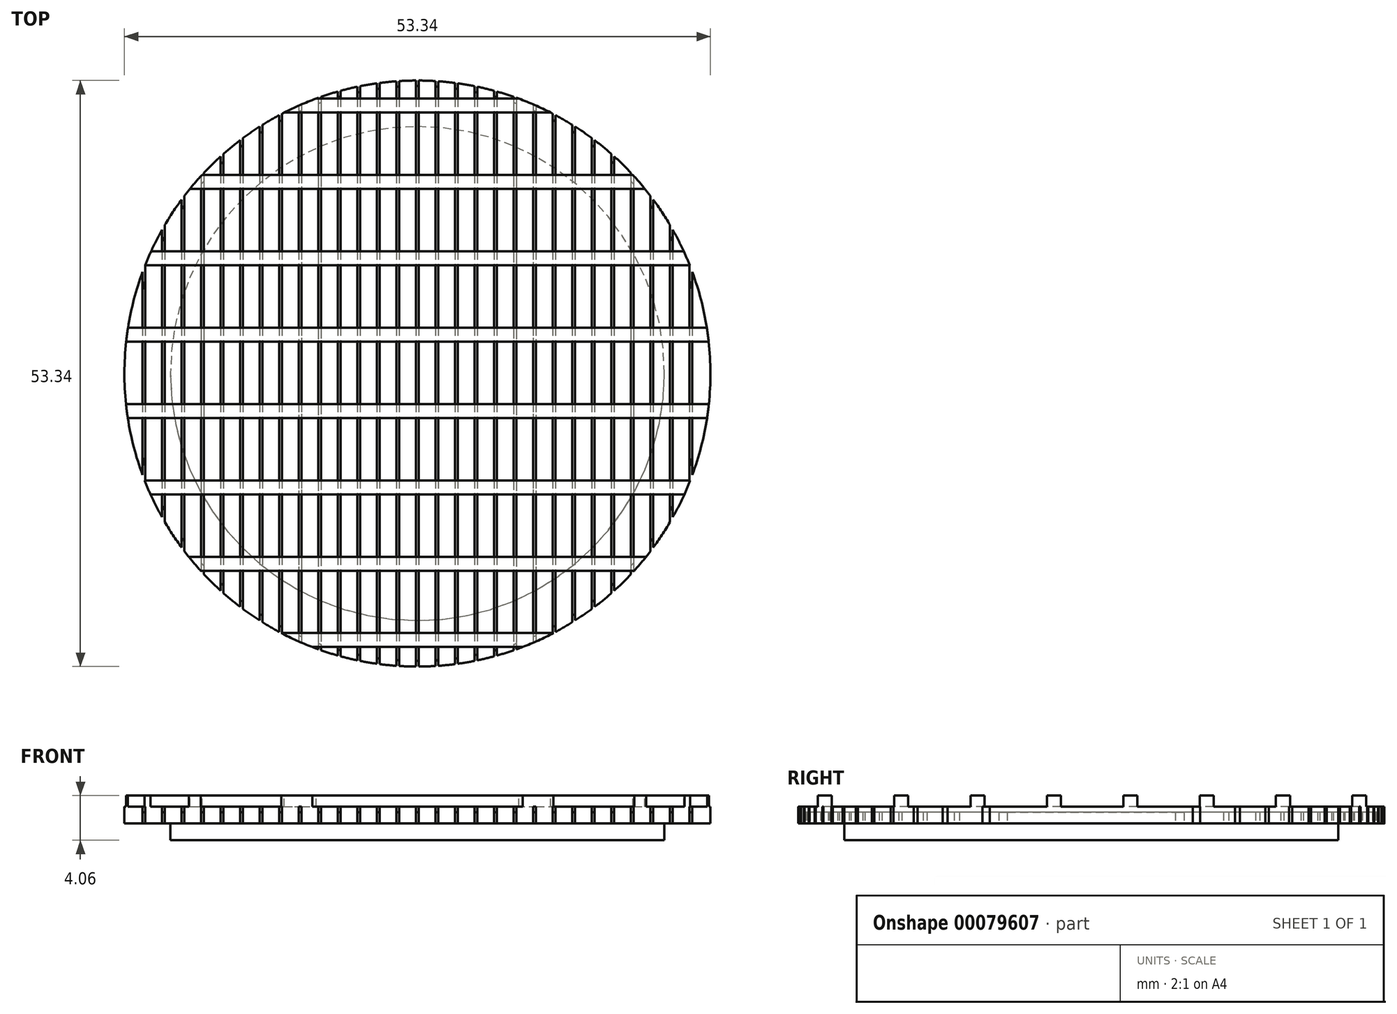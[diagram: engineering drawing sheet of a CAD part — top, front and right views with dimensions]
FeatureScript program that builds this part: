
annotation { "Feature Type Name" : "Feature", "Feature Type Description" : "" }
export const myFeature = defineFeature(function(context is Context, id is Id, definition is map)
    precondition{}
    {
        {
            var Q0;
            Q0=qCreatedBy(makeId("Top.planeOp"),FACE);
            var sketch = newSketch(context, id + "F0", { "sketchPlane" : qUnion([Q0])});
            skCircle(sketch, "E0", {"center": v(0, 0) * mm, "radius": 26.67 * mm});
            skSolve(sketch);
        }
        {
            var Q0;
            Q0 = qSketchRegion(id + "F0", true);
            extrude(context, id + "F1", {"entities" : qUnion([Q0]), "depth" : 1.52 * mm});
        }
        {
            var Q0;
            Q0=makeQuery(id+"F1.opExtrude","CAP_FACE",FACE,{"disambiguationData":[OSD([sQuery(id+"F0.wireOp",EDGE,"E0")])],"isStart":false});
            var sketch = newSketch(context, id + "F2", { "sketchPlane" : qUnion([Q0])});
            skLineSegment(sketch, "E1.bottom", {"start": v(-0.13, 27.42) * mm, "end": v(0.13, 27.42) * mm});
            skLineSegment(sketch, "E1.top", {"start": v(-0.13, -28.46) * mm, "end": v(0.13, -28.46) * mm});
            skLineSegment(sketch, "E1.left", {"start": v(-0.13, 27.42) * mm, "end": v(-0.13, -28.46) * mm});
            skLineSegment(sketch, "E1.right", {"start": v(0.13, 27.42) * mm, "end": v(0.13, -28.46) * mm});
            skLineSegment(sketch, "E2.1.0.0", {"start": v(1.65, 27.42) * mm, "end": v(1.9, 27.42) * mm});
            skLineSegment(sketch, "E2.1.0.1", {"start": v(1.9, 27.42) * mm, "end": v(1.9, -28.46) * mm});
            skLineSegment(sketch, "E2.1.0.2", {"start": v(1.65, 27.42) * mm, "end": v(1.65, -28.46) * mm});
            skLineSegment(sketch, "E2.1.0.3", {"start": v(1.65, -28.46) * mm, "end": v(1.9, -28.46) * mm});
            skLineSegment(sketch, "E2.2.0.0", {"start": v(3.43, 27.42) * mm, "end": v(3.68, 27.42) * mm});
            skLineSegment(sketch, "E2.2.0.1", {"start": v(3.68, 27.42) * mm, "end": v(3.68, -28.46) * mm});
            skLineSegment(sketch, "E2.2.0.2", {"start": v(3.43, 27.42) * mm, "end": v(3.43, -28.46) * mm});
            skLineSegment(sketch, "E2.2.0.3", {"start": v(3.43, -28.46) * mm, "end": v(3.68, -28.46) * mm});
            skLineSegment(sketch, "E2.3.0.0", {"start": v(5.2, 27.42) * mm, "end": v(5.46, 27.42) * mm});
            skLineSegment(sketch, "E2.3.0.1", {"start": v(5.46, 27.42) * mm, "end": v(5.46, -28.46) * mm});
            skLineSegment(sketch, "E2.3.0.2", {"start": v(5.2, 27.42) * mm, "end": v(5.2, -28.46) * mm});
            skLineSegment(sketch, "E2.3.0.3", {"start": v(5.2, -28.46) * mm, "end": v(5.46, -28.46) * mm});
            skLineSegment(sketch, "E2.4.0.0", {"start": v(6.98, 27.42) * mm, "end": v(7.24, 27.42) * mm});
            skLineSegment(sketch, "E2.4.0.1", {"start": v(7.24, 27.42) * mm, "end": v(7.24, -28.46) * mm});
            skLineSegment(sketch, "E2.4.0.2", {"start": v(6.98, 27.42) * mm, "end": v(6.99, -28.46) * mm});
            skLineSegment(sketch, "E2.4.0.3", {"start": v(6.99, -28.46) * mm, "end": v(7.24, -28.46) * mm});
            skLineSegment(sketch, "E2.5.0.0", {"start": v(8.76, 27.42) * mm, "end": v(9.02, 27.42) * mm});
            skLineSegment(sketch, "E2.5.0.1", {"start": v(9.02, 27.42) * mm, "end": v(9.02, -28.46) * mm});
            skLineSegment(sketch, "E2.5.0.2", {"start": v(8.76, 27.42) * mm, "end": v(8.76, -28.46) * mm});
            skLineSegment(sketch, "E2.5.0.3", {"start": v(8.76, -28.46) * mm, "end": v(9.02, -28.46) * mm});
            skLineSegment(sketch, "E2.6.0.0", {"start": v(10.54, 27.42) * mm, "end": v(10.8, 27.42) * mm});
            skLineSegment(sketch, "E2.6.0.1", {"start": v(10.8, 27.42) * mm, "end": v(10.8, -28.46) * mm});
            skLineSegment(sketch, "E2.6.0.2", {"start": v(10.54, 27.42) * mm, "end": v(10.54, -28.46) * mm});
            skLineSegment(sketch, "E2.6.0.3", {"start": v(10.54, -28.46) * mm, "end": v(10.8, -28.46) * mm});
            skLineSegment(sketch, "E2.7.0.0", {"start": v(12.32, 27.42) * mm, "end": v(12.57, 27.42) * mm});
            skLineSegment(sketch, "E2.7.0.1", {"start": v(12.57, 27.42) * mm, "end": v(12.57, -28.46) * mm});
            skLineSegment(sketch, "E2.7.0.2", {"start": v(12.32, 27.42) * mm, "end": v(12.32, -28.46) * mm});
            skLineSegment(sketch, "E2.7.0.3", {"start": v(12.32, -28.46) * mm, "end": v(12.57, -28.46) * mm});
            skLineSegment(sketch, "E2.8.0.0", {"start": v(14.1, 27.42) * mm, "end": v(14.35, 27.42) * mm});
            skLineSegment(sketch, "E2.8.0.1", {"start": v(14.35, 27.42) * mm, "end": v(14.35, -28.46) * mm});
            skLineSegment(sketch, "E2.8.0.2", {"start": v(14.1, 27.42) * mm, "end": v(14.1, -28.46) * mm});
            skLineSegment(sketch, "E2.8.0.3", {"start": v(14.1, -28.46) * mm, "end": v(14.35, -28.46) * mm});
            skLineSegment(sketch, "E2.9.0.0", {"start": v(15.88, 27.42) * mm, "end": v(16.13, 27.42) * mm});
            skLineSegment(sketch, "E2.9.0.1", {"start": v(16.13, 27.42) * mm, "end": v(16.13, -28.46) * mm});
            skLineSegment(sketch, "E2.9.0.2", {"start": v(15.88, 27.42) * mm, "end": v(15.88, -28.46) * mm});
            skLineSegment(sketch, "E2.9.0.3", {"start": v(15.88, -28.46) * mm, "end": v(16.13, -28.46) * mm});
            skLineSegment(sketch, "E2.10.0.0", {"start": v(17.65, 27.42) * mm, "end": v(17.9, 27.42) * mm});
            skLineSegment(sketch, "E2.10.0.1", {"start": v(17.9, 27.42) * mm, "end": v(17.9, -28.46) * mm});
            skLineSegment(sketch, "E2.10.0.2", {"start": v(17.65, 27.42) * mm, "end": v(17.65, -28.46) * mm});
            skLineSegment(sketch, "E2.10.0.3", {"start": v(17.65, -28.46) * mm, "end": v(17.9, -28.46) * mm});
            skLineSegment(sketch, "E2.11.0.0", {"start": v(19.43, 27.42) * mm, "end": v(19.69, 27.42) * mm});
            skLineSegment(sketch, "E2.11.0.1", {"start": v(19.69, 27.42) * mm, "end": v(19.69, -28.46) * mm});
            skLineSegment(sketch, "E2.11.0.2", {"start": v(19.43, 27.42) * mm, "end": v(19.43, -28.46) * mm});
            skLineSegment(sketch, "E2.11.0.3", {"start": v(19.43, -28.46) * mm, "end": v(19.69, -28.46) * mm});
            skLineSegment(sketch, "E2.12.0.0", {"start": v(21.2, 27.42) * mm, "end": v(21.46, 27.42) * mm});
            skLineSegment(sketch, "E2.12.0.1", {"start": v(21.46, 27.42) * mm, "end": v(21.46, -28.46) * mm});
            skLineSegment(sketch, "E2.12.0.2", {"start": v(21.2, 27.42) * mm, "end": v(21.2, -28.46) * mm});
            skLineSegment(sketch, "E2.12.0.3", {"start": v(21.2, -28.46) * mm, "end": v(21.46, -28.46) * mm});
            skLineSegment(sketch, "E2.13.0.0", {"start": v(22.99, 27.42) * mm, "end": v(23.24, 27.42) * mm});
            skLineSegment(sketch, "E2.13.0.1", {"start": v(23.24, 27.42) * mm, "end": v(23.24, -28.46) * mm});
            skLineSegment(sketch, "E2.13.0.2", {"start": v(22.99, 27.42) * mm, "end": v(22.99, -28.46) * mm});
            skLineSegment(sketch, "E2.13.0.3", {"start": v(22.99, -28.46) * mm, "end": v(23.24, -28.46) * mm});
            skLineSegment(sketch, "E2.14.0.0", {"start": v(24.77, 27.42) * mm, "end": v(25.02, 27.42) * mm});
            skLineSegment(sketch, "E2.14.0.1", {"start": v(25.02, 27.42) * mm, "end": v(25.02, -28.46) * mm});
            skLineSegment(sketch, "E2.14.0.2", {"start": v(24.77, 27.42) * mm, "end": v(24.77, -28.46) * mm});
            skLineSegment(sketch, "E2.14.0.3", {"start": v(24.77, -28.46) * mm, "end": v(25.02, -28.46) * mm});
            skLineSegment(sketch, "E2.direction1", {"start": v(-0.13, 27.42) * mm, "end": v(1.65, 27.42) * mm, "construction": true});
            skLineSegment(sketch, "E3.1.0.0", {"start": v(-1.9, 27.42) * mm, "end": v(-1.65, 27.42) * mm});
            skLineSegment(sketch, "E3.1.0.1", {"start": v(-1.9, 27.42) * mm, "end": v(-1.9, -28.46) * mm});
            skLineSegment(sketch, "E3.1.0.2", {"start": v(-1.65, 27.42) * mm, "end": v(-1.65, -28.46) * mm});
            skLineSegment(sketch, "E3.1.0.3", {"start": v(-1.9, -28.46) * mm, "end": v(-1.65, -28.46) * mm});
            skLineSegment(sketch, "E3.2.0.0", {"start": v(-3.68, 27.42) * mm, "end": v(-3.43, 27.42) * mm});
            skLineSegment(sketch, "E3.2.0.1", {"start": v(-3.68, 27.42) * mm, "end": v(-3.68, -28.46) * mm});
            skLineSegment(sketch, "E3.2.0.2", {"start": v(-3.43, 27.42) * mm, "end": v(-3.43, -28.46) * mm});
            skLineSegment(sketch, "E3.2.0.3", {"start": v(-3.68, -28.46) * mm, "end": v(-3.43, -28.46) * mm});
            skLineSegment(sketch, "E3.3.0.0", {"start": v(-5.46, 27.42) * mm, "end": v(-5.2, 27.42) * mm});
            skLineSegment(sketch, "E3.3.0.1", {"start": v(-5.46, 27.42) * mm, "end": v(-5.46, -28.46) * mm});
            skLineSegment(sketch, "E3.3.0.2", {"start": v(-5.2, 27.42) * mm, "end": v(-5.2, -28.46) * mm});
            skLineSegment(sketch, "E3.3.0.3", {"start": v(-5.46, -28.46) * mm, "end": v(-5.2, -28.46) * mm});
            skLineSegment(sketch, "E3.4.0.0", {"start": v(-7.24, 27.42) * mm, "end": v(-6.98, 27.42) * mm});
            skLineSegment(sketch, "E3.4.0.1", {"start": v(-7.24, 27.42) * mm, "end": v(-7.24, -28.46) * mm});
            skLineSegment(sketch, "E3.4.0.2", {"start": v(-6.98, 27.42) * mm, "end": v(-6.98, -28.46) * mm});
            skLineSegment(sketch, "E3.4.0.3", {"start": v(-7.24, -28.46) * mm, "end": v(-6.98, -28.46) * mm});
            skLineSegment(sketch, "E3.5.0.0", {"start": v(-9.02, 27.42) * mm, "end": v(-8.76, 27.42) * mm});
            skLineSegment(sketch, "E3.5.0.1", {"start": v(-9.02, 27.42) * mm, "end": v(-9.02, -28.46) * mm});
            skLineSegment(sketch, "E3.5.0.2", {"start": v(-8.76, 27.42) * mm, "end": v(-8.76, -28.46) * mm});
            skLineSegment(sketch, "E3.5.0.3", {"start": v(-9.02, -28.46) * mm, "end": v(-8.76, -28.46) * mm});
            skLineSegment(sketch, "E3.6.0.0", {"start": v(-10.8, 27.42) * mm, "end": v(-10.54, 27.42) * mm});
            skLineSegment(sketch, "E3.6.0.1", {"start": v(-10.8, 27.42) * mm, "end": v(-10.8, -28.46) * mm});
            skLineSegment(sketch, "E3.6.0.2", {"start": v(-10.54, 27.42) * mm, "end": v(-10.54, -28.46) * mm});
            skLineSegment(sketch, "E3.6.0.3", {"start": v(-10.8, -28.46) * mm, "end": v(-10.54, -28.46) * mm});
            skLineSegment(sketch, "E3.7.0.0", {"start": v(-12.57, 27.42) * mm, "end": v(-12.32, 27.42) * mm});
            skLineSegment(sketch, "E3.7.0.1", {"start": v(-12.57, 27.42) * mm, "end": v(-12.57, -28.46) * mm});
            skLineSegment(sketch, "E3.7.0.2", {"start": v(-12.32, 27.42) * mm, "end": v(-12.32, -28.46) * mm});
            skLineSegment(sketch, "E3.7.0.3", {"start": v(-12.57, -28.46) * mm, "end": v(-12.32, -28.46) * mm});
            skLineSegment(sketch, "E3.8.0.0", {"start": v(-14.35, 27.42) * mm, "end": v(-14.1, 27.42) * mm});
            skLineSegment(sketch, "E3.8.0.1", {"start": v(-14.35, 27.42) * mm, "end": v(-14.35, -28.46) * mm});
            skLineSegment(sketch, "E3.8.0.2", {"start": v(-14.1, 27.42) * mm, "end": v(-14.1, -28.46) * mm});
            skLineSegment(sketch, "E3.8.0.3", {"start": v(-14.35, -28.46) * mm, "end": v(-14.1, -28.46) * mm});
            skLineSegment(sketch, "E3.9.0.0", {"start": v(-16.13, 27.42) * mm, "end": v(-15.87, 27.42) * mm});
            skLineSegment(sketch, "E3.9.0.1", {"start": v(-16.13, 27.42) * mm, "end": v(-16.13, -28.46) * mm});
            skLineSegment(sketch, "E3.9.0.2", {"start": v(-15.87, 27.42) * mm, "end": v(-15.87, -28.46) * mm});
            skLineSegment(sketch, "E3.9.0.3", {"start": v(-16.13, -28.46) * mm, "end": v(-15.87, -28.46) * mm});
            skLineSegment(sketch, "E3.10.0.0", {"start": v(-17.9, 27.42) * mm, "end": v(-17.65, 27.42) * mm});
            skLineSegment(sketch, "E3.10.0.1", {"start": v(-17.9, 27.42) * mm, "end": v(-17.9, -28.46) * mm});
            skLineSegment(sketch, "E3.10.0.2", {"start": v(-17.65, 27.42) * mm, "end": v(-17.65, -28.46) * mm});
            skLineSegment(sketch, "E3.10.0.3", {"start": v(-17.9, -28.46) * mm, "end": v(-17.65, -28.46) * mm});
            skLineSegment(sketch, "E3.11.0.0", {"start": v(-19.68, 27.42) * mm, "end": v(-19.43, 27.42) * mm});
            skLineSegment(sketch, "E3.11.0.1", {"start": v(-19.68, 27.42) * mm, "end": v(-19.68, -28.46) * mm});
            skLineSegment(sketch, "E3.11.0.2", {"start": v(-19.43, 27.42) * mm, "end": v(-19.43, -28.46) * mm});
            skLineSegment(sketch, "E3.11.0.3", {"start": v(-19.68, -28.46) * mm, "end": v(-19.43, -28.46) * mm});
            skLineSegment(sketch, "E3.12.0.0", {"start": v(-21.46, 27.42) * mm, "end": v(-21.2, 27.42) * mm});
            skLineSegment(sketch, "E3.12.0.1", {"start": v(-21.46, 27.42) * mm, "end": v(-21.46, -28.46) * mm});
            skLineSegment(sketch, "E3.12.0.2", {"start": v(-21.2, 27.42) * mm, "end": v(-21.2, -28.46) * mm});
            skLineSegment(sketch, "E3.12.0.3", {"start": v(-21.46, -28.46) * mm, "end": v(-21.2, -28.46) * mm});
            skLineSegment(sketch, "E3.13.0.0", {"start": v(-23.24, 27.42) * mm, "end": v(-22.99, 27.42) * mm});
            skLineSegment(sketch, "E3.13.0.1", {"start": v(-23.24, 27.42) * mm, "end": v(-23.24, -28.46) * mm});
            skLineSegment(sketch, "E3.13.0.2", {"start": v(-22.99, 27.42) * mm, "end": v(-22.99, -28.46) * mm});
            skLineSegment(sketch, "E3.13.0.3", {"start": v(-23.24, -28.46) * mm, "end": v(-22.99, -28.46) * mm});
            skLineSegment(sketch, "E3.14.0.0", {"start": v(-25.02, 27.42) * mm, "end": v(-24.76, 27.42) * mm});
            skLineSegment(sketch, "E3.14.0.1", {"start": v(-25.02, 27.42) * mm, "end": v(-25.02, -28.46) * mm});
            skLineSegment(sketch, "E3.14.0.2", {"start": v(-24.76, 27.42) * mm, "end": v(-24.76, -28.46) * mm});
            skLineSegment(sketch, "E3.14.0.3", {"start": v(-25.02, -28.46) * mm, "end": v(-24.76, -28.46) * mm});
            skLineSegment(sketch, "E3.direction1", {"start": v(-0.13, 27.42) * mm, "end": v(-1.9, 27.42) * mm, "construction": true});
            skSolve(sketch);
        }
        {
            var Q0;
            Q0 = qSketchRegion(id + "F2", true);
            extrude(context, id + "F3", {"entities" : qUnion([Q0]), "operationType" : NewBodyOperationType.REMOVE, "endBound" : BoundingType.THROUGH_ALL, "oppositeDirection" : true, "depth" : 0.5 * mm});
        }
        {
            var Q0;
            Q0=qCreatedBy(makeId("Top.planeOp"),FACE);
            var sketch = newSketch(context, id + "F4", { "sketchPlane" : qUnion([Q0])});
            skCircle(sketch, "E4", {"center": v(0, 0) * mm, "radius": 26.16 * mm});
            skSolve(sketch);
        }
        {
            var Q0;
            Q0 = qSketchRegion(id + "F4", true);
            extrude(context, id + "F5", {"entities" : qUnion([Q0]), "operationType" : NewBodyOperationType.ADD, "depth" : 1.02 * mm});
        }
        {
            var Q0;
            {var subQ0=sQuery(id+"F0.wireOp",EDGE,"E0");var subQ2=makeQuery(id+"F1.opExtrude","CAP_FACE",FACE,{"disambiguationData":[OSD([subQ0])],"isStart":true});Q0=makeQuery(id+"F5.boolean.opBoolean","MERGE",FACE,{"derivedFrom":[makeQuery(id+"F3.boolean.opBoolean","SPLIT",FACE,{"disambiguationData":[TD([makeQuery(id+"F3.opExtrude","SWEPT_FACE",FACE,{"disambiguationData":[OSD([sQuery(id+"F2.wireOp",EDGE,"E2.14.0.1")])]})])],"derivedFrom":subQ2}),makeQuery(id+"F3.boolean.opBoolean","SPLIT",FACE,{"disambiguationData":[TD([makeQuery(id+"F3.opExtrude","SWEPT_FACE",FACE,{"disambiguationData":[OSD([sQuery(id+"F2.wireOp",EDGE,"E3.14.0.1")])]})])],"derivedFrom":subQ2}),makeQuery(id+"F3.boolean.opBoolean","SPLIT",FACE,{"disambiguationData":[TD([makeQuery(id+"F3.opExtrude","SWEPT_FACE",FACE,{"disambiguationData":[OSD([sQuery(id+"F2.wireOp",EDGE,"E1.left")])]})])],"derivedFrom":subQ2}),makeQuery(id+"F3.boolean.opBoolean","SPLIT",FACE,{"disambiguationData":[TD([makeQuery(id+"F3.opExtrude","SWEPT_FACE",FACE,{"disambiguationData":[OSD([sQuery(id+"F2.wireOp",EDGE,"E1.right")])]})])],"derivedFrom":subQ2}),makeQuery(id+"F3.boolean.opBoolean","SPLIT",FACE,{"disambiguationData":[TD([makeQuery(id+"F3.opExtrude","SWEPT_FACE",FACE,{"disambiguationData":[OSD([sQuery(id+"F2.wireOp",EDGE,"E2.1.0.1")])]})])],"derivedFrom":subQ2}),makeQuery(id+"F3.boolean.opBoolean","SPLIT",FACE,{"disambiguationData":[TD([makeQuery(id+"F3.opExtrude","SWEPT_FACE",FACE,{"disambiguationData":[OSD([sQuery(id+"F2.wireOp",EDGE,"E2.2.0.1")])]})])],"derivedFrom":subQ2}),makeQuery(id+"F3.boolean.opBoolean","SPLIT",FACE,{"disambiguationData":[TD([makeQuery(id+"F3.opExtrude","SWEPT_FACE",FACE,{"disambiguationData":[OSD([sQuery(id+"F2.wireOp",EDGE,"E2.3.0.1")])]})])],"derivedFrom":subQ2}),makeQuery(id+"F3.boolean.opBoolean","SPLIT",FACE,{"disambiguationData":[TD([makeQuery(id+"F3.opExtrude","SWEPT_FACE",FACE,{"disambiguationData":[OSD([sQuery(id+"F2.wireOp",EDGE,"E2.4.0.1")])]})])],"derivedFrom":subQ2}),makeQuery(id+"F3.boolean.opBoolean","SPLIT",FACE,{"disambiguationData":[TD([makeQuery(id+"F3.opExtrude","SWEPT_FACE",FACE,{"disambiguationData":[OSD([sQuery(id+"F2.wireOp",EDGE,"E2.5.0.1")])]})])],"derivedFrom":subQ2}),makeQuery(id+"F3.boolean.opBoolean","SPLIT",FACE,{"disambiguationData":[TD([makeQuery(id+"F3.opExtrude","SWEPT_FACE",FACE,{"disambiguationData":[OSD([sQuery(id+"F2.wireOp",EDGE,"E2.6.0.1")])]})])],"derivedFrom":subQ2}),makeQuery(id+"F3.boolean.opBoolean","SPLIT",FACE,{"disambiguationData":[TD([makeQuery(id+"F3.opExtrude","SWEPT_FACE",FACE,{"disambiguationData":[OSD([sQuery(id+"F2.wireOp",EDGE,"E2.7.0.1")])]})])],"derivedFrom":subQ2}),makeQuery(id+"F3.boolean.opBoolean","SPLIT",FACE,{"disambiguationData":[TD([makeQuery(id+"F3.opExtrude","SWEPT_FACE",FACE,{"disambiguationData":[OSD([sQuery(id+"F2.wireOp",EDGE,"E2.8.0.1")])]})])],"derivedFrom":subQ2}),makeQuery(id+"F3.boolean.opBoolean","SPLIT",FACE,{"disambiguationData":[TD([makeQuery(id+"F3.opExtrude","SWEPT_FACE",FACE,{"disambiguationData":[OSD([sQuery(id+"F2.wireOp",EDGE,"E2.9.0.1")])]})])],"derivedFrom":subQ2}),makeQuery(id+"F3.boolean.opBoolean","SPLIT",FACE,{"disambiguationData":[TD([makeQuery(id+"F3.opExtrude","SWEPT_FACE",FACE,{"disambiguationData":[OSD([sQuery(id+"F2.wireOp",EDGE,"E2.10.0.1")])]})])],"derivedFrom":subQ2}),makeQuery(id+"F3.boolean.opBoolean","SPLIT",FACE,{"disambiguationData":[TD([makeQuery(id+"F3.opExtrude","SWEPT_FACE",FACE,{"disambiguationData":[OSD([sQuery(id+"F2.wireOp",EDGE,"E2.11.0.1")])]})])],"derivedFrom":subQ2}),makeQuery(id+"F3.boolean.opBoolean","SPLIT",FACE,{"disambiguationData":[TD([makeQuery(id+"F3.opExtrude","SWEPT_FACE",FACE,{"disambiguationData":[OSD([sQuery(id+"F2.wireOp",EDGE,"E2.12.0.1")])]})])],"derivedFrom":subQ2}),makeQuery(id+"F3.boolean.opBoolean","SPLIT",FACE,{"disambiguationData":[TD([makeQuery(id+"F3.opExtrude","SWEPT_FACE",FACE,{"disambiguationData":[OSD([sQuery(id+"F2.wireOp",EDGE,"E2.13.0.1")])]})])],"derivedFrom":subQ2}),makeQuery(id+"F3.boolean.opBoolean","SPLIT",FACE,{"disambiguationData":[TD([makeQuery(id+"F3.opExtrude","SWEPT_FACE",FACE,{"disambiguationData":[OSD([sQuery(id+"F2.wireOp",EDGE,"E3.1.0.1")])]})])],"derivedFrom":subQ2}),makeQuery(id+"F3.boolean.opBoolean","SPLIT",FACE,{"disambiguationData":[TD([makeQuery(id+"F3.opExtrude","SWEPT_FACE",FACE,{"disambiguationData":[OSD([sQuery(id+"F2.wireOp",EDGE,"E3.2.0.1")])]})])],"derivedFrom":subQ2}),makeQuery(id+"F3.boolean.opBoolean","SPLIT",FACE,{"disambiguationData":[TD([makeQuery(id+"F3.opExtrude","SWEPT_FACE",FACE,{"disambiguationData":[OSD([sQuery(id+"F2.wireOp",EDGE,"E3.3.0.1")])]})])],"derivedFrom":subQ2}),makeQuery(id+"F3.boolean.opBoolean","SPLIT",FACE,{"disambiguationData":[TD([makeQuery(id+"F3.opExtrude","SWEPT_FACE",FACE,{"disambiguationData":[OSD([sQuery(id+"F2.wireOp",EDGE,"E3.4.0.1")])]})])],"derivedFrom":subQ2}),makeQuery(id+"F3.boolean.opBoolean","SPLIT",FACE,{"disambiguationData":[TD([makeQuery(id+"F3.opExtrude","SWEPT_FACE",FACE,{"disambiguationData":[OSD([sQuery(id+"F2.wireOp",EDGE,"E3.5.0.1")])]})])],"derivedFrom":subQ2}),makeQuery(id+"F3.boolean.opBoolean","SPLIT",FACE,{"disambiguationData":[TD([makeQuery(id+"F3.opExtrude","SWEPT_FACE",FACE,{"disambiguationData":[OSD([sQuery(id+"F2.wireOp",EDGE,"E3.6.0.1")])]})])],"derivedFrom":subQ2}),makeQuery(id+"F3.boolean.opBoolean","SPLIT",FACE,{"disambiguationData":[TD([makeQuery(id+"F3.opExtrude","SWEPT_FACE",FACE,{"disambiguationData":[OSD([sQuery(id+"F2.wireOp",EDGE,"E3.7.0.1")])]})])],"derivedFrom":subQ2}),makeQuery(id+"F3.boolean.opBoolean","SPLIT",FACE,{"disambiguationData":[TD([makeQuery(id+"F3.opExtrude","SWEPT_FACE",FACE,{"disambiguationData":[OSD([sQuery(id+"F2.wireOp",EDGE,"E3.8.0.1")])]})])],"derivedFrom":subQ2}),makeQuery(id+"F3.boolean.opBoolean","SPLIT",FACE,{"disambiguationData":[TD([makeQuery(id+"F3.opExtrude","SWEPT_FACE",FACE,{"disambiguationData":[OSD([sQuery(id+"F2.wireOp",EDGE,"E3.9.0.1")])]})])],"derivedFrom":subQ2}),makeQuery(id+"F3.boolean.opBoolean","SPLIT",FACE,{"disambiguationData":[TD([makeQuery(id+"F3.opExtrude","SWEPT_FACE",FACE,{"disambiguationData":[OSD([sQuery(id+"F2.wireOp",EDGE,"E3.10.0.1")])]})])],"derivedFrom":subQ2}),makeQuery(id+"F3.boolean.opBoolean","SPLIT",FACE,{"disambiguationData":[TD([makeQuery(id+"F3.opExtrude","SWEPT_FACE",FACE,{"disambiguationData":[OSD([sQuery(id+"F2.wireOp",EDGE,"E3.11.0.1")])]})])],"derivedFrom":subQ2}),makeQuery(id+"F3.boolean.opBoolean","SPLIT",FACE,{"disambiguationData":[TD([makeQuery(id+"F3.opExtrude","SWEPT_FACE",FACE,{"disambiguationData":[OSD([sQuery(id+"F2.wireOp",EDGE,"E3.12.0.1")])]})])],"derivedFrom":subQ2}),makeQuery(id+"F3.boolean.opBoolean","SPLIT",FACE,{"disambiguationData":[TD([makeQuery(id+"F3.opExtrude","SWEPT_FACE",FACE,{"disambiguationData":[OSD([sQuery(id+"F2.wireOp",EDGE,"E3.13.0.1")])]})])],"derivedFrom":subQ2}),makeQuery(id+"F5.opExtrude","CAP_FACE",FACE,{"disambiguationData":[OSD([sQuery(id+"F4.wireOp",EDGE,"E4")])],"isStart":true})]});}
            var sketch = newSketch(context, id + "F6", { "sketchPlane" : qUnion([Q0])});
            skCircle(sketch, "E5", {"center": v(0, 0) * mm, "radius": 22.48 * mm});
            skSolve(sketch);
        }
        {
            var Q0;
            Q0 = qSketchRegion(id + "F6", true);
            extrude(context, id + "F7", {"entities" : qUnion([Q0]), "operationType" : NewBodyOperationType.ADD, "depth" : 1.52 * mm});
        }
        {
            var Q0;
            {var subQ0=sQuery(id+"F0.wireOp",EDGE,"E0");Q0=makeQuery(id+"F3.boolean.opBoolean","SPLIT",FACE,{"disambiguationData":[TD([makeQuery(id+"F3.opExtrude","SWEPT_FACE",FACE,{"disambiguationData":[OSD([sQuery(id+"F2.wireOp",EDGE,"E3.14.0.1")])]})])],"derivedFrom":makeQuery(id+"F1.opExtrude","CAP_FACE",FACE,{"disambiguationData":[OSD([subQ0])],"isStart":false})});}
            var sketch = newSketch(context, id + "F8", { "sketchPlane" : qUnion([Q0])});
            skLineSegment(sketch, "E6.bottom", {"start": v(-28.07, -23.62) * mm, "end": v(27.81, -23.62) * mm});
            skLineSegment(sketch, "E6.top", {"start": v(-28.07, -24.9) * mm, "end": v(27.81, -24.9) * mm});
            skLineSegment(sketch, "E6.left", {"start": v(-28.07, -23.62) * mm, "end": v(-28.07, -24.9) * mm});
            skLineSegment(sketch, "E6.right", {"start": v(27.81, -23.62) * mm, "end": v(27.81, -24.9) * mm});
            skLineSegment(sketch, "E7.0.1.0", {"start": v(-28.07, -16.67) * mm, "end": v(27.81, -16.67) * mm});
            skLineSegment(sketch, "E7.0.1.1", {"start": v(-28.07, -17.94) * mm, "end": v(27.81, -17.94) * mm});
            skLineSegment(sketch, "E7.0.1.2", {"start": v(27.81, -16.67) * mm, "end": v(27.81, -17.94) * mm});
            skLineSegment(sketch, "E7.0.1.3", {"start": v(-28.07, -16.67) * mm, "end": v(-28.07, -17.94) * mm});
            skLineSegment(sketch, "E7.0.2.0", {"start": v(-28.07, -9.72) * mm, "end": v(27.81, -9.72) * mm});
            skLineSegment(sketch, "E7.0.2.1", {"start": v(-28.07, -11) * mm, "end": v(27.81, -11) * mm});
            skLineSegment(sketch, "E7.0.2.2", {"start": v(27.81, -9.72) * mm, "end": v(27.81, -11) * mm});
            skLineSegment(sketch, "E7.0.2.3", {"start": v(-28.07, -9.72) * mm, "end": v(-28.07, -11) * mm});
            skLineSegment(sketch, "E7.0.3.0", {"start": v(-28.07, -2.77) * mm, "end": v(27.81, -2.77) * mm});
            skLineSegment(sketch, "E7.0.3.1", {"start": v(-28.07, -4.04) * mm, "end": v(27.81, -4.04) * mm});
            skLineSegment(sketch, "E7.0.3.2", {"start": v(27.81, -2.77) * mm, "end": v(27.81, -4.04) * mm});
            skLineSegment(sketch, "E7.0.3.3", {"start": v(-28.07, -2.77) * mm, "end": v(-28.07, -4.04) * mm});
            skLineSegment(sketch, "E7.0.4.0", {"start": v(-28.07, 4.18) * mm, "end": v(27.81, 4.18) * mm});
            skLineSegment(sketch, "E7.0.4.1", {"start": v(-28.07, 2.9) * mm, "end": v(27.81, 2.9) * mm});
            skLineSegment(sketch, "E7.0.4.2", {"start": v(27.81, 4.18) * mm, "end": v(27.81, 2.9) * mm});
            skLineSegment(sketch, "E7.0.4.3", {"start": v(-28.07, 4.18) * mm, "end": v(-28.07, 2.9) * mm});
            skLineSegment(sketch, "E7.0.5.0", {"start": v(-28.07, 11.13) * mm, "end": v(27.81, 11.13) * mm});
            skLineSegment(sketch, "E7.0.5.1", {"start": v(-28.07, 9.86) * mm, "end": v(27.81, 9.86) * mm});
            skLineSegment(sketch, "E7.0.5.2", {"start": v(27.81, 11.13) * mm, "end": v(27.81, 9.86) * mm});
            skLineSegment(sketch, "E7.0.5.3", {"start": v(-28.07, 11.13) * mm, "end": v(-28.07, 9.86) * mm});
            skLineSegment(sketch, "E7.0.6.0", {"start": v(-28.07, 18.07) * mm, "end": v(27.81, 18.07) * mm});
            skLineSegment(sketch, "E7.0.6.1", {"start": v(-28.07, 16.8) * mm, "end": v(27.81, 16.8) * mm});
            skLineSegment(sketch, "E7.0.6.2", {"start": v(27.81, 18.07) * mm, "end": v(27.81, 16.8) * mm});
            skLineSegment(sketch, "E7.0.6.3", {"start": v(-28.07, 18.07) * mm, "end": v(-28.07, 16.8) * mm});
            skLineSegment(sketch, "E7.0.7.0", {"start": v(-28.07, 25.02) * mm, "end": v(27.81, 25.02) * mm});
            skLineSegment(sketch, "E7.0.7.1", {"start": v(-28.07, 23.75) * mm, "end": v(27.81, 23.75) * mm});
            skLineSegment(sketch, "E7.0.7.2", {"start": v(27.81, 25.02) * mm, "end": v(27.81, 23.75) * mm});
            skLineSegment(sketch, "E7.0.7.3", {"start": v(-28.07, 25.02) * mm, "end": v(-28.07, 23.75) * mm});
            skLineSegment(sketch, "E7.direction1", {"start": v(-28.07, -23.62) * mm, "end": v(-2.67, -23.62) * mm, "construction": true});
            skLineSegment(sketch, "E7.direction2", {"start": v(-28.07, -23.62) * mm, "end": v(-28.07, -16.67) * mm, "construction": true});
            skSolve(sketch);
        }
        {
            var Q0;
            Q0 = qSketchRegion(id + "F8", true);
            extrude(context, id + "F9", {"entities" : qUnion([Q0]), "operationType" : NewBodyOperationType.ADD, "depth" : 1.02 * mm});
        }
        {
            var Q0;
            Q0=makeQuery(id+"F9.opExtrude","CAP_FACE",FACE,{"disambiguationData":[OSD([sQuery(id+"F8.wireOp",EDGE,"E7.0.7.0"),sQuery(id+"F8.wireOp",EDGE,"E7.0.7.1"),sQuery(id+"F8.wireOp",EDGE,"E7.0.7.2"),sQuery(id+"F8.wireOp",EDGE,"E7.0.7.3")])],"isStart":false});
            var sketch = newSketch(context, id + "F10", { "sketchPlane" : qUnion([Q0])});
            skCircle(sketch, "E8", {"center": v(0, 0) * mm, "radius": 26.67 * mm});
            skCircle(sketch, "E9", {"center": v(0, 0) * mm, "radius": 42.25 * mm});
            skSolve(sketch);
        }
        {
            var Q0;
            Q0 = qSketchRegion(id + "F10", true);
            extrude(context, id + "F11", {"entities" : qUnion([Q0]), "operationType" : NewBodyOperationType.REMOVE, "oppositeDirection" : true, "depth" : 25.4 * mm});
        }
    });
